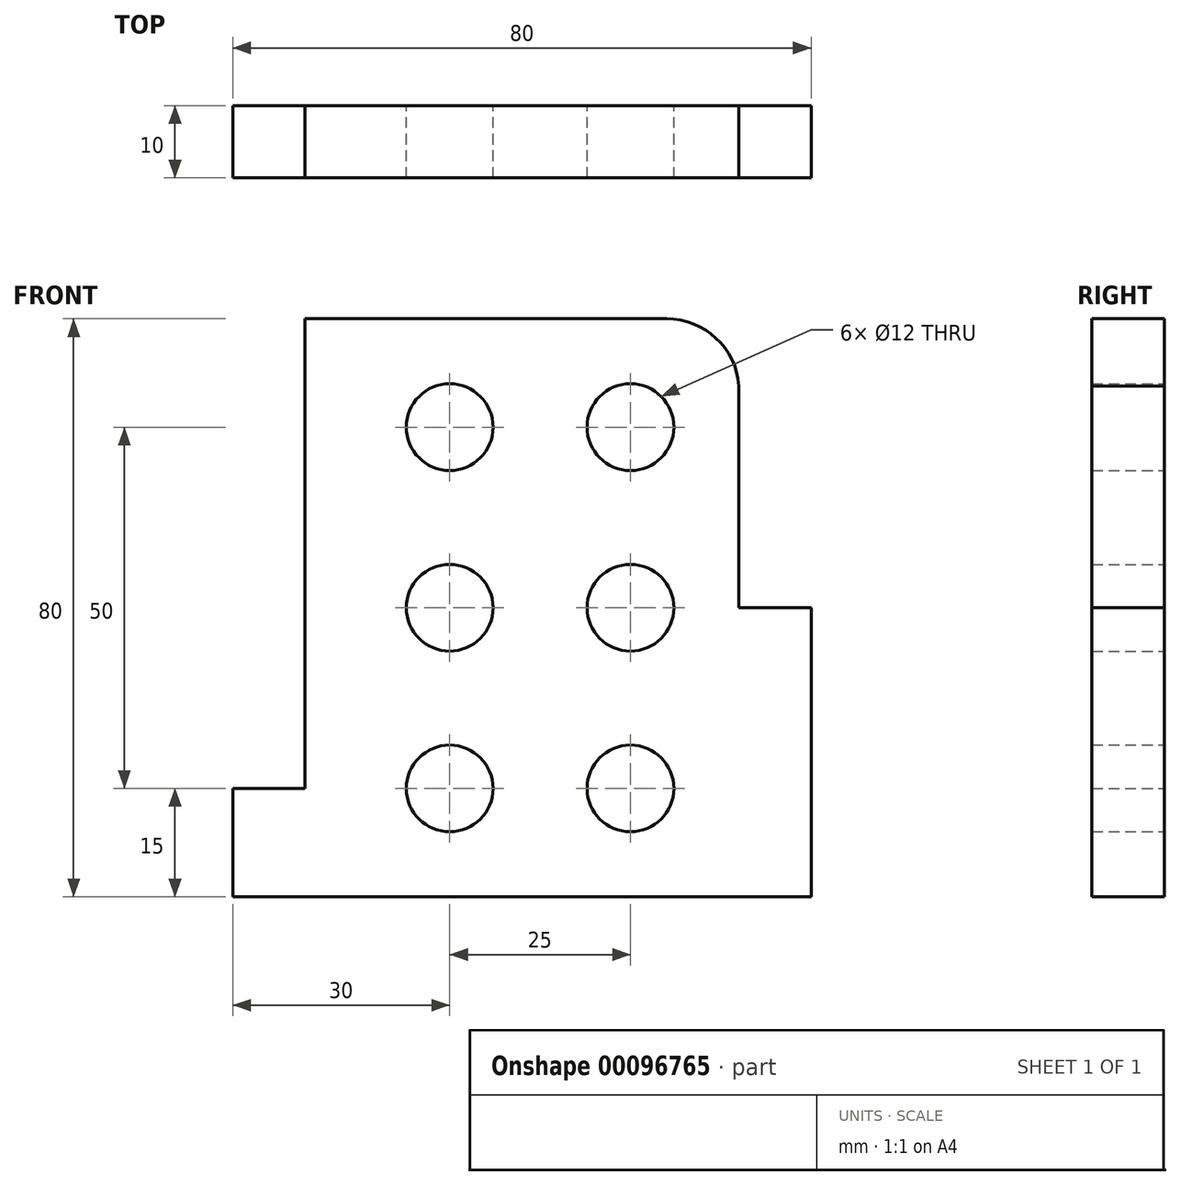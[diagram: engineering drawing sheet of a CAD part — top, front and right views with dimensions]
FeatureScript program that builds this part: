
annotation { "Feature Type Name" : "Feature", "Feature Type Description" : "" }
export const myFeature = defineFeature(function(context is Context, id is Id, definition is map)
    precondition{}
    {
        {
            var Q0;
            Q0=qCreatedBy(makeId("Front.planeOp"),FACE);
            var sketch = newSketch(context, id + "F0", { "sketchPlane" : qUnion([Q0])});
            skLineSegment(sketch, "E0", {"start": v(0, 0) * mm, "end": v(0, 15) * mm});
            skLineSegment(sketch, "E1", {"start": v(0, 15) * mm, "end": v(10, 15) * mm});
            skLineSegment(sketch, "E2", {"start": v(10, 15) * mm, "end": v(10, 80) * mm});
            skLineSegment(sketch, "E3", {"start": v(70, 40) * mm, "end": v(80, 40) * mm});
            skLineSegment(sketch, "E4", {"start": v(80, 40) * mm, "end": v(80, 0) * mm});
            skLineSegment(sketch, "E5", {"start": v(80, 0) * mm, "end": v(0, 0) * mm});
            skLineSegment(sketch, "E6", {"start": v(70, 70.71) * mm, "end": v(70, 40) * mm});
            skLineSegment(sketch, "E7", {"start": v(10, 80) * mm, "end": v(60.03, 80) * mm});
            skCircle(sketch, "E8", {"center": v(30, 65) * mm, "radius": 6 * mm});
            skCircle(sketch, "E9", {"center": v(55, 65) * mm, "radius": 6 * mm});
            skCircle(sketch, "E10", {"center": v(30, 40) * mm, "radius": 6 * mm});
            skCircle(sketch, "E11", {"center": v(55, 40) * mm, "radius": 6 * mm});
            skCircle(sketch, "E12", {"center": v(30, 15) * mm, "radius": 6 * mm});
            skCircle(sketch, "E13", {"center": v(55, 15) * mm, "radius": 6 * mm});
            skArc(sketch, "E14", {"start": v(70, 70.71) * mm, "mid": v(66.84, 77.32) * mm, "end": v(60.03, 80) * mm});
            skSolve(sketch);
        }
        {
            var Q0;
            Q0=makeQuery(id+"F0.imprint","IMPRINT",FACE,{"disambiguationData":[TD([[makeQuery(id+"F0.imprint","IMPRINT",EDGE,{"derivedFrom":sQuery(id+"F0.wireOp",EDGE,"E0")}),-1.0]])]});
            extrude(context, id + "F1", {"entities" : qUnion([Q0]), "depth" : 10 * mm});
        }
    });
